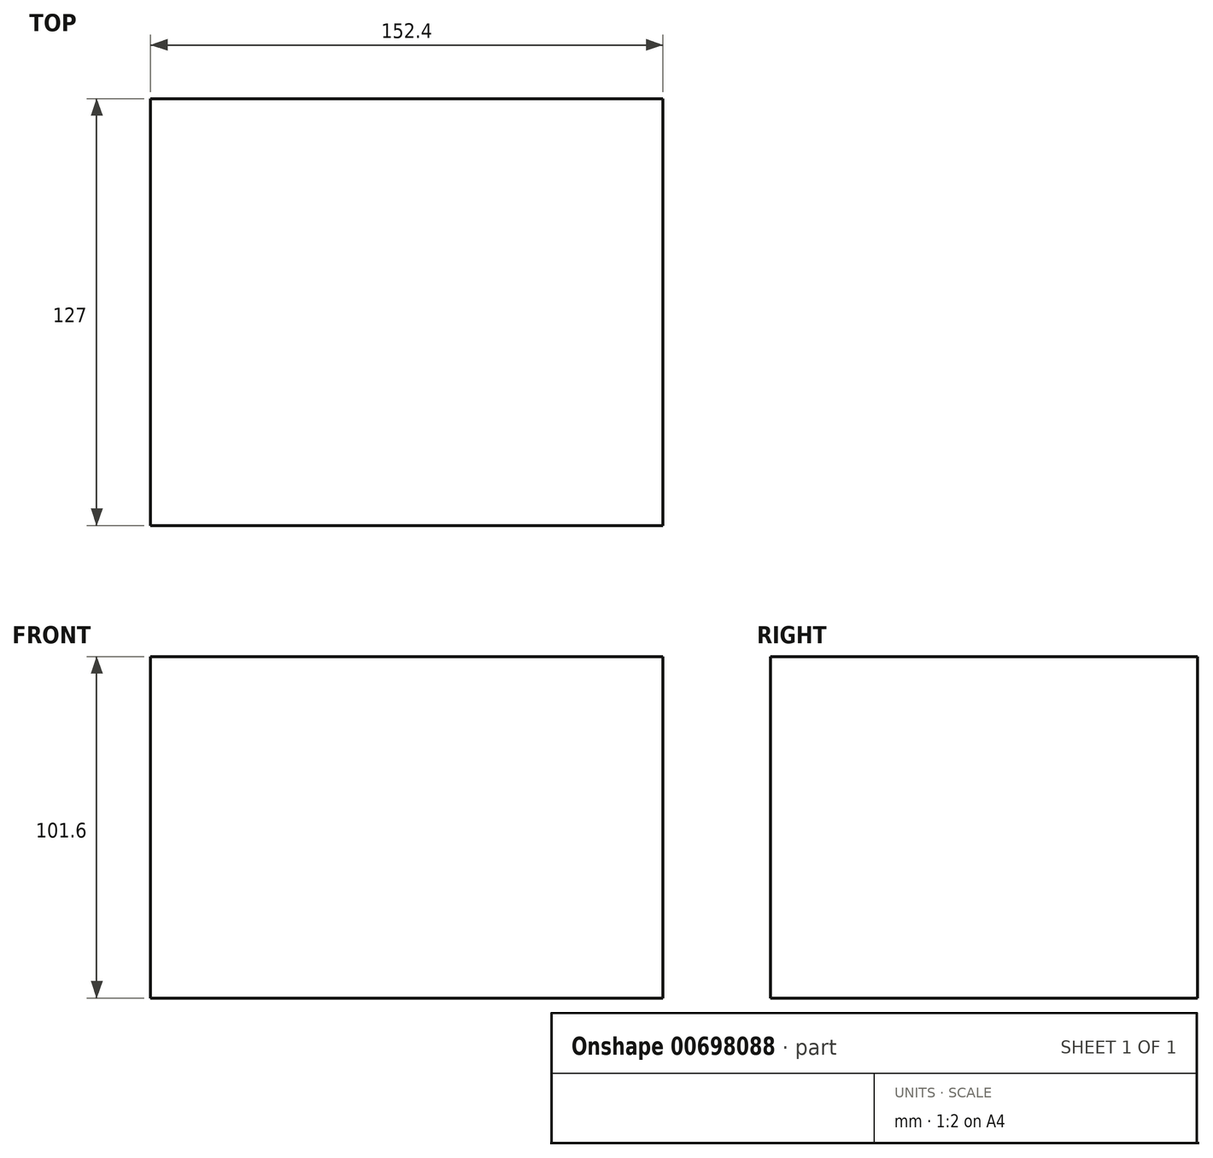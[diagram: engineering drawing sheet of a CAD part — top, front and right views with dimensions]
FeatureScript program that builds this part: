
annotation { "Feature Type Name" : "Feature", "Feature Type Description" : "" }
export const myFeature = defineFeature(function(context is Context, id is Id, definition is map)
    precondition{}
    {
        {
            var Q0;
            Q0=qCreatedBy(makeId("Front.planeOp"),FACE);
            var sketch = newSketch(context, id + "F0", { "sketchPlane" : qUnion([Q0])});
            skLineSegment(sketch, "E0.bottom", {"start": v(-71.1, -32.27) * mm, "end": v(81.3, -32.27) * mm});
            skLineSegment(sketch, "E0.top", {"start": v(-71.1, 69.33) * mm, "end": v(81.3, 69.33) * mm});
            skLineSegment(sketch, "E0.left", {"start": v(-71.1, -32.27) * mm, "end": v(-71.1, 69.33) * mm});
            skLineSegment(sketch, "E0.right", {"start": v(81.3, -32.27) * mm, "end": v(81.3, 69.33) * mm});
            skSolve(sketch);
        }
        {
            var Q0;
            Q0 = qSketchRegion(id + "F0", true);
            extrude(context, id + "F1", {"entities" : qUnion([Q0]), "depth" : 127 * mm, "offsetDistance" : 25.4 * mm});
        }
    });
